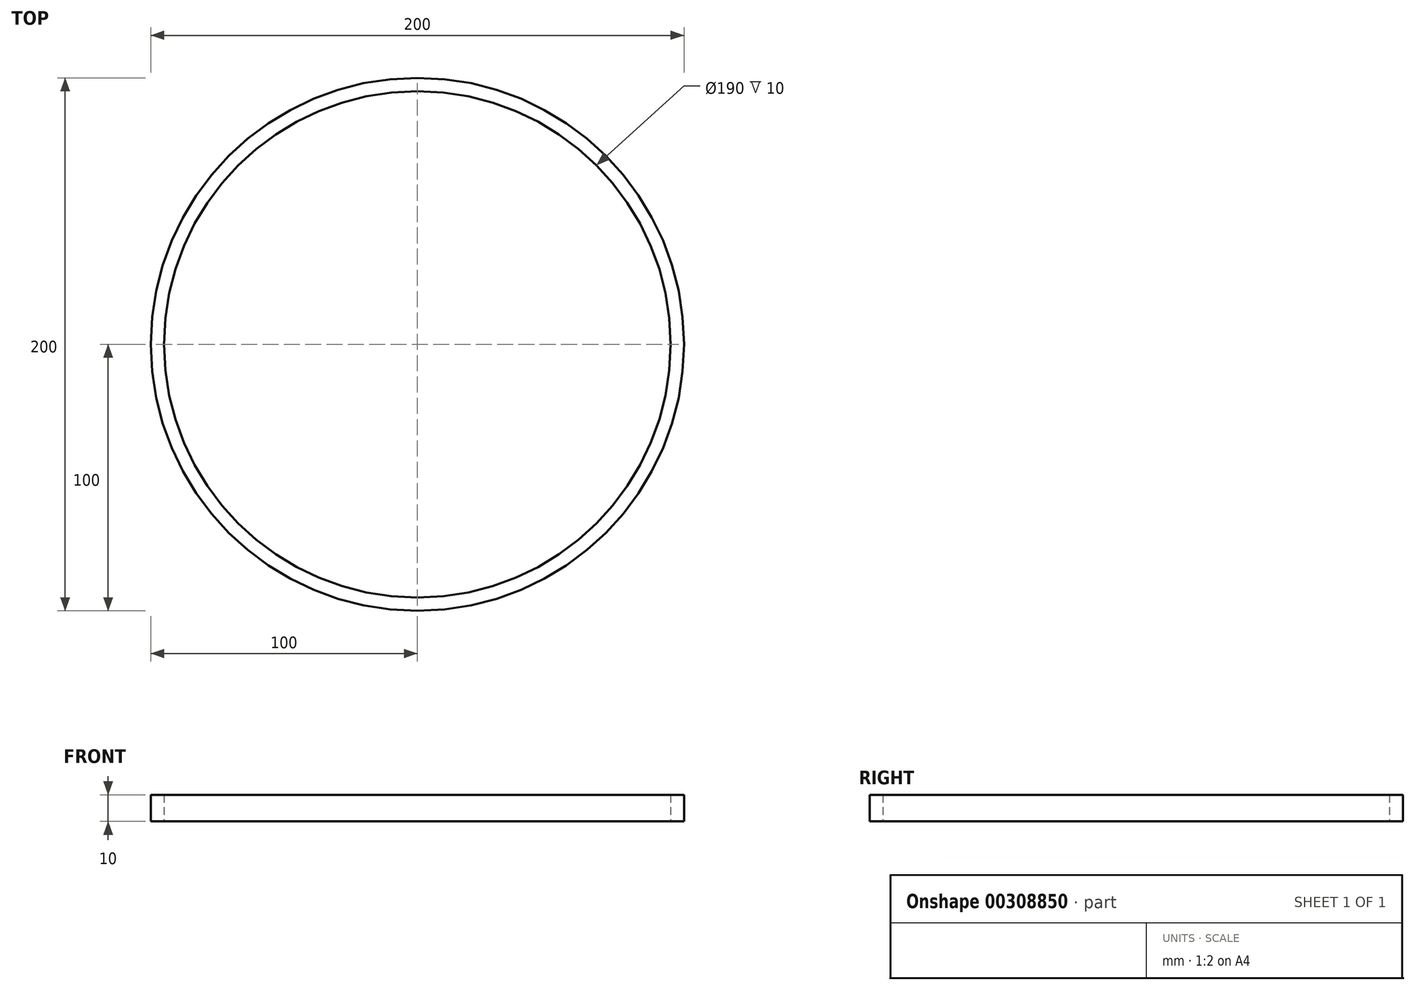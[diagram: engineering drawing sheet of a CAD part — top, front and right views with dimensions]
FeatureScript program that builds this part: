
annotation { "Feature Type Name" : "Feature", "Feature Type Description" : "" }
export const myFeature = defineFeature(function(context is Context, id is Id, definition is map)
    precondition{}
    {
        {
            var Q0;
            Q0=qCreatedBy(makeId("Top.planeOp"),FACE);
            var sketch = newSketch(context, id + "F0", { "sketchPlane" : qUnion([Q0])});
            skCircle(sketch, "E0", {"center": v(0, 0) * mm, "radius": 100 * mm});
            skCircle(sketch, "E1", {"center": v(0, 0) * mm, "radius": 95 * mm});
            skSolve(sketch);
        }
        {
            var Q0;
            Q0=makeQuery(id+"F0.imprint","IMPRINT",FACE,{"disambiguationData":[TD([[makeQuery(id+"F0.imprint","IMPRINT",EDGE,{"derivedFrom":sQuery(id+"F0.wireOp",EDGE,"E0")}),1.0]])]});
            extrude(context, id + "F1", {"entities" : qUnion([Q0]), "depth" : 10 * mm});
        }
    });
